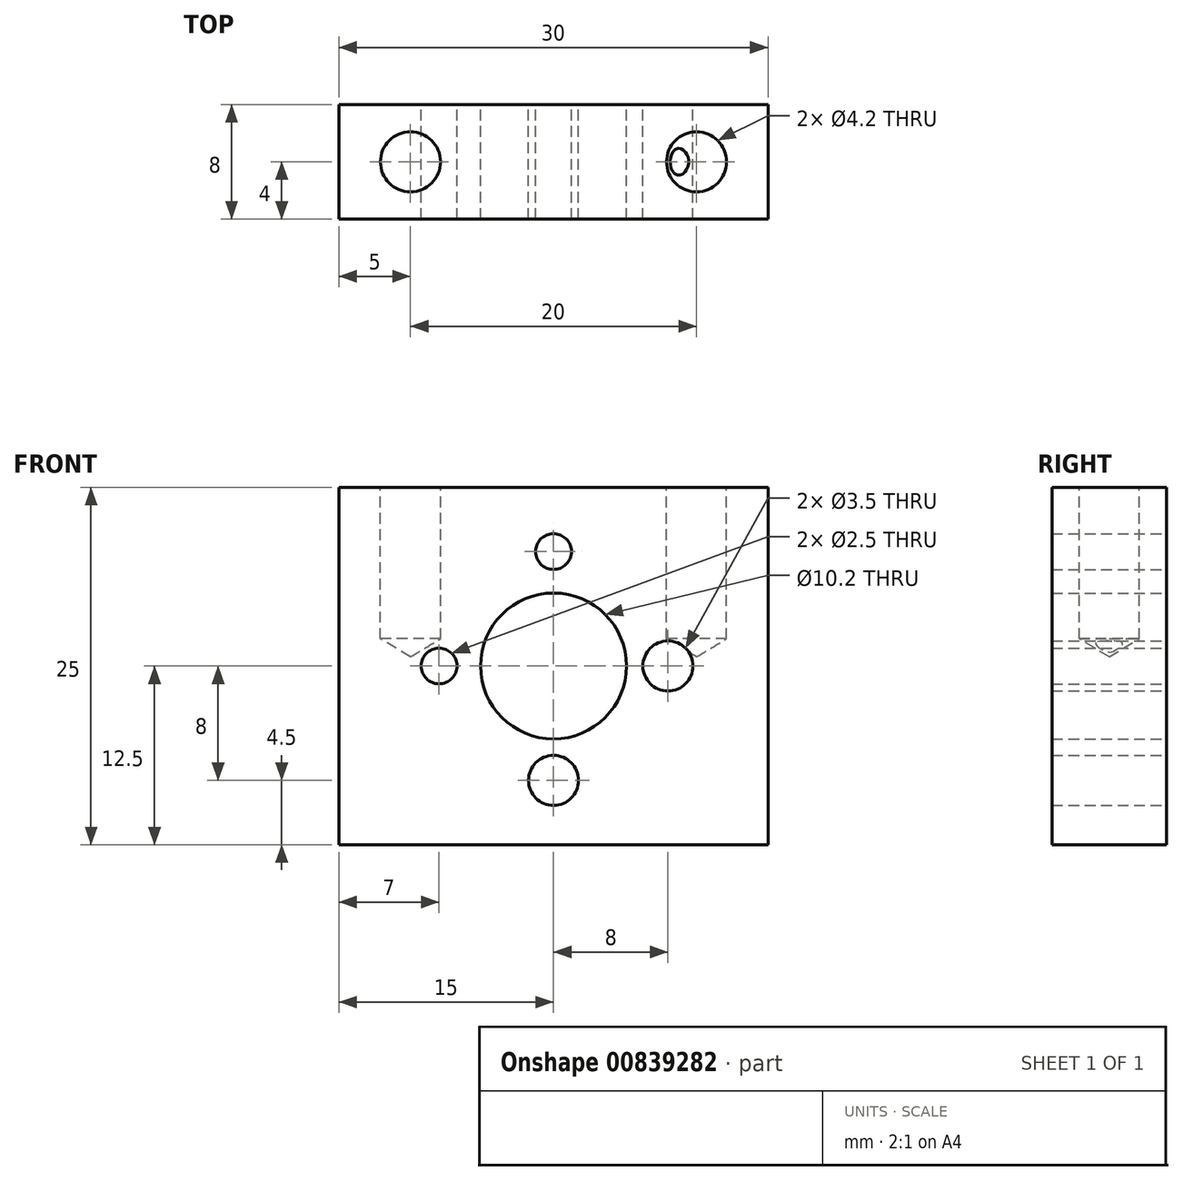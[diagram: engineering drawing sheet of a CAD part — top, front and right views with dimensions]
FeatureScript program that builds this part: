
annotation { "Feature Type Name" : "Feature", "Feature Type Description" : "" }
export const myFeature = defineFeature(function(context is Context, id is Id, definition is map)
    precondition{}
    {
        {
            var Q0;
            Q0=qCreatedBy(makeId("Front.planeOp"),FACE);
            var sketch = newSketch(context, id + "F0", { "sketchPlane" : qUnion([Q0])});
            skCircle(sketch, "E0", {"center": v(0, 0) * mm, "radius": 5.1 * mm});
            skCircle(sketch, "E1", {"center": v(0, 0) * mm, "radius": 8 * mm});
            skCircle(sketch, "E2", {"center": v(0, 8) * mm, "radius": 1.75 * mm});
            skCircle(sketch, "E3", {"center": v(8, 0) * mm, "radius": 1.75 * mm});
            skCircle(sketch, "E4", {"center": v(0, -8) * mm, "radius": 1.75 * mm});
            skCircle(sketch, "E5", {"center": v(-8, 0) * mm, "radius": 1.75 * mm});
            skLineSegment(sketch, "E6", {"start": v(0, -9.75) * mm, "end": v(0, -12.5) * mm});
            skLineSegment(sketch, "E7", {"start": v(0, -12.5) * mm, "end": v(15, -12.5) * mm});
            skLineSegment(sketch, "E8", {"start": v(0, 9.75) * mm, "end": v(0, 12.5) * mm});
            skLineSegment(sketch, "E9", {"start": v(0, 12.5) * mm, "end": v(15, 12.5) * mm});
            skLineSegment(sketch, "E10", {"start": v(15, 12.5) * mm, "end": v(15, -12.5) * mm});
            skLineSegment(sketch, "E11.MirrorCS", {"start": v(0, 12.5) * mm, "end": v(-15, 12.5) * mm});
            skLineSegment(sketch, "E12.MirrorCS", {"start": v(-15, 12.5) * mm, "end": v(-15, -12.5) * mm});
            skLineSegment(sketch, "E13.MirrorCS", {"start": v(0, -12.5) * mm, "end": v(-15, -12.5) * mm});
            skSolve(sketch);
        }
        {
            var Q0;
            {var subQ1=sQuery(id+"F0.wireOp",EDGE,"E6");Q0=makeQuery(id+"F0.imprint","IMPRINT",FACE,{"disambiguationData":[TD([[makeQuery(id+"F0.imprint","IMPRINT",EDGE,{"derivedFrom":subQ1}),-1.0]])]});}
            var Q1;
            {var subQ1=sQuery(id+"F0.wireOp",EDGE,"E6");Q1=makeQuery(id+"F0.imprint","IMPRINT",FACE,{"disambiguationData":[TD([[makeQuery(id+"F0.imprint","IMPRINT",EDGE,{"derivedFrom":subQ1}),1.0]])]});}
            var Q2;
            Q2=makeQuery(id+"F0.imprint","IMPRINT",FACE,{"disambiguationData":[TD([[makeQuery(id+"F0.imprint","IMPRINT",EDGE,{"derivedFrom":sQuery(id+"F0.wireOp",EDGE,"E0")}),-1.0]])]});
            var Q3;
            {var subQ0=sQuery(id+"F0.wireOp",EDGE,"E2");var subQ1=sQuery(id+"F0.wireOp",EDGE,"E1");var subQ2=makeQuery(id+"F0.imprint","INTERSECT",VERTEX,{"disambiguationData":[OD(0.0)],"derivedFrom":[subQ1,subQ0]});Q3=makeQuery(id+"F0.imprint","IMPRINT",FACE,{"disambiguationData":[TD([[makeQuery(id+"F0.imprint","IMPRINT",EDGE,{"disambiguationData":[TD([[subQ2,-1.0]])],"derivedFrom":subQ1}),-1.0]])]});}
            var Q4;
            {var subQ0=sQuery(id+"F0.wireOp",EDGE,"E5");var subQ1=sQuery(id+"F0.wireOp",EDGE,"E1");var subQ2=makeQuery(id+"F0.imprint","INTERSECT",VERTEX,{"disambiguationData":[OD(0.0)],"derivedFrom":[subQ1,subQ0]});Q4=makeQuery(id+"F0.imprint","IMPRINT",FACE,{"disambiguationData":[TD([[makeQuery(id+"F0.imprint","IMPRINT",EDGE,{"disambiguationData":[TD([[subQ2,-1.0]])],"derivedFrom":subQ1}),-1.0]])]});}
            var Q5;
            {var subQ0=sQuery(id+"F0.wireOp",EDGE,"E5");var subQ1=sQuery(id+"F0.wireOp",EDGE,"E1");var subQ2=makeQuery(id+"F0.imprint","INTERSECT",VERTEX,{"disambiguationData":[OD(0.0)],"derivedFrom":[subQ1,subQ0]});Q5=makeQuery(id+"F0.imprint","IMPRINT",FACE,{"disambiguationData":[TD([[makeQuery(id+"F0.imprint","IMPRINT",EDGE,{"disambiguationData":[TD([[subQ2,-1.0]])],"derivedFrom":subQ1}),1.0]])]});}
            var Q6;
            {var subQ0=sQuery(id+"F0.wireOp",EDGE,"E3");var subQ1=sQuery(id+"F0.wireOp",EDGE,"E1");var subQ2=makeQuery(id+"F0.imprint","INTERSECT",VERTEX,{"disambiguationData":[OD(0.0)],"derivedFrom":[subQ1,subQ0]});Q6=makeQuery(id+"F0.imprint","IMPRINT",FACE,{"disambiguationData":[TD([[makeQuery(id+"F0.imprint","IMPRINT",EDGE,{"disambiguationData":[TD([[subQ2,1.0]])],"derivedFrom":subQ1}),-1.0]])]});}
            var Q7;
            {var subQ0=sQuery(id+"F0.wireOp",EDGE,"E3");var subQ1=sQuery(id+"F0.wireOp",EDGE,"E1");var subQ2=makeQuery(id+"F0.imprint","INTERSECT",VERTEX,{"disambiguationData":[OD(0.0)],"derivedFrom":[subQ1,subQ0]});Q7=makeQuery(id+"F0.imprint","IMPRINT",FACE,{"disambiguationData":[TD([[makeQuery(id+"F0.imprint","IMPRINT",EDGE,{"disambiguationData":[TD([[subQ2,1.0]])],"derivedFrom":subQ1}),1.0]])]});}
            var Q8;
            {var subQ0=sQuery(id+"F0.wireOp",EDGE,"E4");var subQ1=sQuery(id+"F0.wireOp",EDGE,"E1");var subQ2=makeQuery(id+"F0.imprint","INTERSECT",VERTEX,{"disambiguationData":[OD(0.0)],"derivedFrom":[subQ1,subQ0]});Q8=makeQuery(id+"F0.imprint","IMPRINT",FACE,{"disambiguationData":[TD([[makeQuery(id+"F0.imprint","IMPRINT",EDGE,{"disambiguationData":[TD([[subQ2,-1.0]])],"derivedFrom":subQ1}),1.0]])]});}
            var Q9;
            {var subQ0=sQuery(id+"F0.wireOp",EDGE,"E4");var subQ1=sQuery(id+"F0.wireOp",EDGE,"E1");var subQ2=makeQuery(id+"F0.imprint","INTERSECT",VERTEX,{"disambiguationData":[OD(0.0)],"derivedFrom":[subQ1,subQ0]});Q9=makeQuery(id+"F0.imprint","IMPRINT",FACE,{"disambiguationData":[TD([[makeQuery(id+"F0.imprint","IMPRINT",EDGE,{"disambiguationData":[TD([[subQ2,-1.0]])],"derivedFrom":subQ1}),-1.0]])]});}
            var Q10;
            {var subQ0=sQuery(id+"F0.wireOp",EDGE,"E2");var subQ1=sQuery(id+"F0.wireOp",EDGE,"E1");var subQ2=makeQuery(id+"F0.imprint","INTERSECT",VERTEX,{"disambiguationData":[OD(0.0)],"derivedFrom":[subQ1,subQ0]});Q10=makeQuery(id+"F0.imprint","IMPRINT",FACE,{"disambiguationData":[TD([[makeQuery(id+"F0.imprint","IMPRINT",EDGE,{"disambiguationData":[TD([[subQ2,-1.0]])],"derivedFrom":subQ1}),1.0]])]});}
            extrude(context, id + "F1", {"entities" : qUnion([Q0, Q1, Q2, Q3, Q4, Q5, Q6, Q7, Q8, Q9, Q10]), "depth" : 8 * mm, "offsetDistance" : 25 * mm});
        }
        {
            var Q0;
            Q0=makeQuery(id+"F1.opExtrude","SWEPT_FACE",FACE,{"disambiguationData":[OSD([sQuery(id+"F0.wireOp",EDGE,"E9"),sQuery(id+"F0.wireOp",EDGE,"E11.MirrorCS")])]});
            var sketch = newSketch(context, id + "F2", { "sketchPlane" : qUnion([Q0])});
            skCircle(sketch, "E14", {"center": v(-10, -4) * mm, "radius": 2.15 * mm});
            skCircle(sketch, "E15.MirrorC", {"center": v(10, -4) * mm, "radius": 2.15 * mm});
            skSolve(sketch);
        }
        {
            var Q0;
            Q0=sQuery(id+"F0.wireOp",VERTEX,"E2.center");
            var Q1;
            Q1=sQuery(id+"F0.wireOp",VERTEX,"E3.center");
            var Q2;
            Q2=sQuery(id+"F0.wireOp",VERTEX,"E5.center");
            var Q3;
            Q3=sQuery(id+"F0.wireOp",VERTEX,"E4.center");
            var Q4;
            Q4=makeQuery(id+"F1.opExtrude","SWEPT_BODY",BODY,{"disambiguationData":[OSD([sQuery(id+"F0.wireOp",EDGE,"E0"),sQuery(id+"F0.wireOp",EDGE,"E7"),sQuery(id+"F0.wireOp",EDGE,"E9"),sQuery(id+"F0.wireOp",EDGE,"E10"),sQuery(id+"F0.wireOp",EDGE,"E11.MirrorCS"),sQuery(id+"F0.wireOp",EDGE,"E12.MirrorCS"),sQuery(id+"F0.wireOp",EDGE,"E13.MirrorCS")])]});
            hole(context, id + "F3", {"style" : HoleStyle.SIMPLE, "endStyle" : HoleEndStyle.THROUGH, "oppositeDirection" : true, "standardTappedOrClearance" : lookupTablePath({ "standard" : "ISO", "engagement" : "75%", "pitch" : "0.5 mm", "size" : "M3", "type" : "Tapped" }), "standardBlindInLast" : lookupTablePath({ "standard" : "ISO", "fit" : "Normal", "engagement" : "75%", "pitch" : "0.5 mm", "size" : "M3", "type" : "Clearance & tapped" }), "holeDiameter" : 2.5 * mm, "majorDiameter" : 3 * mm, "showTappedDepth" : true, "isTappedThrough" : true, "tappedDepth" : 12 * mm, "tapClearance" : 3, "locations" : qUnion([Q0, Q1, Q2, Q3]), "scope" : qUnion([Q4])});
        }
        {
            var Q0;
            Q0=sQuery(id+"F2.wireOp",VERTEX,"E14.center");
            var Q1;
            Q1=sQuery(id+"F2.wireOp",VERTEX,"E15.MirrorC.center");
            var Q2;
            Q2=makeQuery(id+"F1.opExtrude","SWEPT_BODY",BODY,{"disambiguationData":[OSD([sQuery(id+"F0.wireOp",EDGE,"E0"),sQuery(id+"F0.wireOp",EDGE,"E7"),sQuery(id+"F0.wireOp",EDGE,"E9"),sQuery(id+"F0.wireOp",EDGE,"E10"),sQuery(id+"F0.wireOp",EDGE,"E11.MirrorCS"),sQuery(id+"F0.wireOp",EDGE,"E12.MirrorCS"),sQuery(id+"F0.wireOp",EDGE,"E13.MirrorCS")])]});
            hole(context, id + "F4", {"style" : HoleStyle.SIMPLE, "endStyle" : HoleEndStyle.BLIND, "standardTappedOrClearance" : lookupTablePath({ "standard" : "ISO", "engagement" : "75%", "pitch" : "0.8 mm", "size" : "M5", "type" : "Tapped" }), "standardBlindInLast" : lookupTablePath({ "standard" : "ISO", "fit" : "Normal", "engagement" : "75%", "pitch" : "0.8 mm", "size" : "M5", "type" : "Clearance & tapped" }), "holeDiameter" : 4.2 * mm, "majorDiameter" : 5 * mm, "showTappedDepth" : true, "holeDepth" : 10.6 * mm, "isTappedThrough" : true, "tappedDepth" : 9 * mm, "tapClearance" : 2, "locations" : qUnion([Q0, Q1]), "scope" : qUnion([Q2])});
        }
    });
